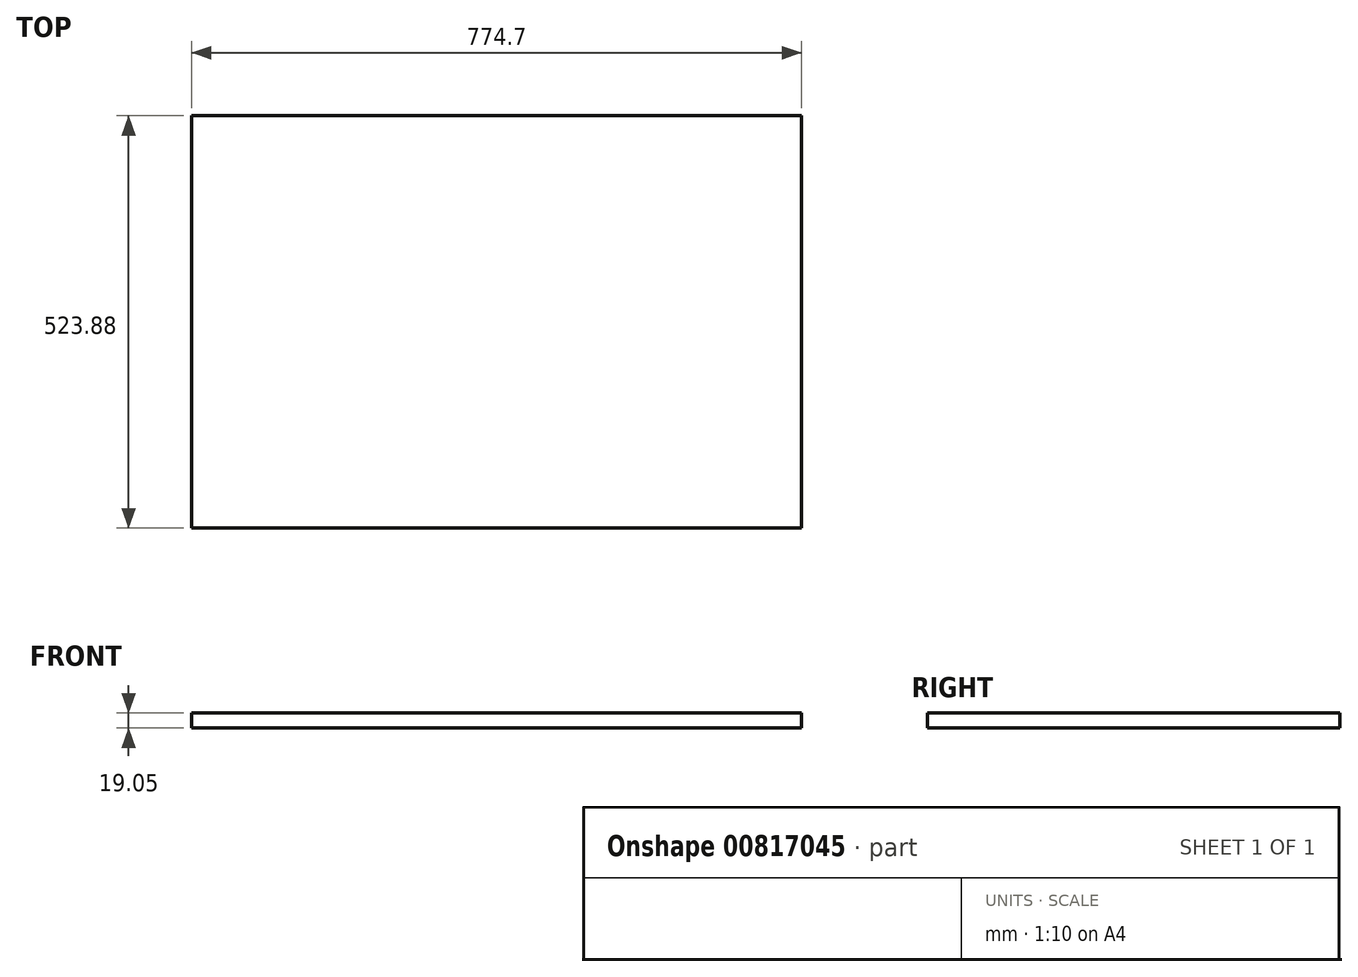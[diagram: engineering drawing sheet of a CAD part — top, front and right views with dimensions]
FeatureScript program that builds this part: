
annotation { "Feature Type Name" : "Feature", "Feature Type Description" : "" }
export const myFeature = defineFeature(function(context is Context, id is Id, definition is map)
    precondition{}
    {
        {
            var Q0;
            Q0=qCreatedBy(makeId("Top.planeOp"),FACE);
            var sketch = newSketch(context, id + "F0", { "sketchPlane" : qUnion([Q0])});
            skLineSegment(sketch, "E0.bottom", {"start": v(387.35, 261.94) * mm, "end": v(-387.35, 261.94) * mm});
            skLineSegment(sketch, "E0.top", {"start": v(387.35, -261.94) * mm, "end": v(-387.35, -261.94) * mm});
            skLineSegment(sketch, "E0.left", {"start": v(387.35, 261.94) * mm, "end": v(387.35, -261.94) * mm});
            skLineSegment(sketch, "E0.right", {"start": v(-387.35, 261.94) * mm, "end": v(-387.35, -261.94) * mm});
            skPoint(sketch, "E0.middle", {"position": v(0, 0) * mm});
            skSolve(sketch);
        }
        {
            var Q0;
            Q0=qSketchRegion(id+"F0",true);
            extrude(context, id + "F1", {"entities" : qUnion([Q0]), "depth" : 19.05 * mm, "offsetDistance" : 25.4 * mm});
        }
    });
